# Revit family: AD-CI52T
name_source: partatom
category: Communication Devices
revit_build: Autodesk Revit Architecture 2012 (Build: 20110309_2315(x64)
units: mm (PartAtom-declared; Revit-internal decimal feet)

## types (1)
- AD-CI52T
    100V Taps = 30, 15, 7.5, 3.8
    70V Taps = 30, 15, 7.5, 3.8
    Coverage Horizontal = 90.00°
    Coverage Vertical = 90.00°
    Default Elevation = 48"
    Depth = 9.56"
    Description = 5.25" Weather Resistant Loudspeaker element
    Enclosure Depth = 7.81"
    Enclosure Radius = 3.423"
    Grille Depth = 0.28"
    Grille Radius Base = 4.25"
    Grille Radius Extent = 3.536"
    Impedance = 8
    Manufacturer = QSC Audio Products, LLC
    Manufacturer URL = www.qscaudio.com
    Middle Depth = 1.47"
    Middle Radius = 3.68"
    Model = AD-CI52T
    Power Handling = 40
    Product Documentation Link = http://media.qscaudio.com
    Product Page URL = http://www.qscaudio.com
    Regulatory Compliance = RoHS
    SPL Max = 102
    Sensitivity = 86
    URL = http://www.qscaudio.com
    Weight Dimensional (kg) = 10.9
    Weight Dimensional (lb) = 24
    Weight Product (kg) = 3.4
    Weight Product (lb) = 7.5
    Width = 8.5"

## geometry (parser evidence)
native form markers: Blend x2, Sweep x1
no freeform markers — native parametric forms only
